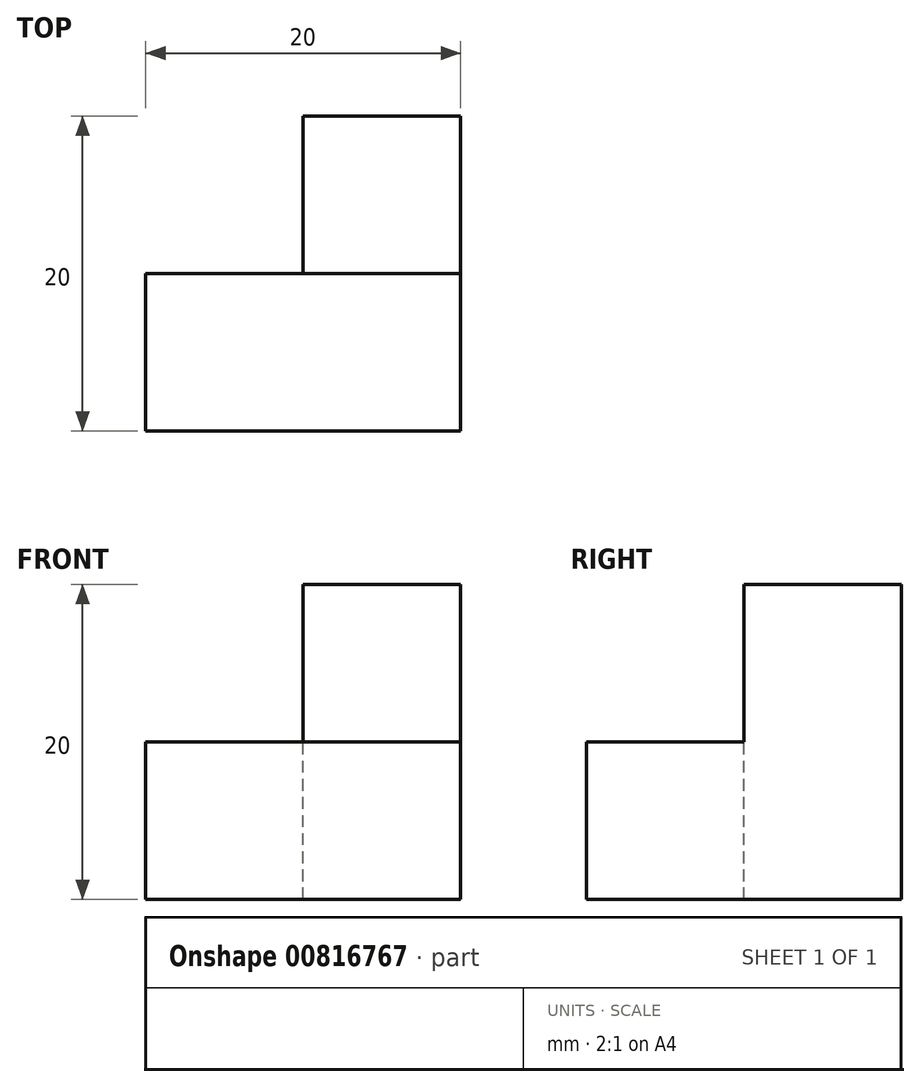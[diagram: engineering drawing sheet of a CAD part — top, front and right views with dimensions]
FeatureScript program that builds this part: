
annotation { "Feature Type Name" : "Feature", "Feature Type Description" : "" }
export const myFeature = defineFeature(function(context is Context, id is Id, definition is map)
    precondition{}
    {
        {
            var Q0;
            Q0=qCreatedBy(makeId("Top.planeOp"),FACE);
            var sketch = newSketch(context, id + "F0", { "sketchPlane" : qUnion([Q0])});
            skLineSegment(sketch, "E0.bottom", {"start": v(0, 0) * mm, "end": v(10, 0) * mm});
            skLineSegment(sketch, "E0.top", {"start": v(0, 10) * mm, "end": v(10, 10) * mm});
            skLineSegment(sketch, "E0.left", {"start": v(0, 0) * mm, "end": v(0, 10) * mm});
            skLineSegment(sketch, "E0.right", {"start": v(10, 0) * mm, "end": v(10, 10) * mm});
            skSolve(sketch);
        }
        {
            var Q0;
            Q0=makeQuery(id+"F0.imprint","IMPRINT",FACE,{"disambiguationData":[TD([[makeQuery(id+"F0.imprint","IMPRINT",EDGE,{"derivedFrom":sQuery(id+"F0.wireOp",EDGE,"E0.bottom")}),1.0]])]});
            extrude(context, id + "F1", {"entities" : qUnion([Q0]), "depth" : 20 * mm, "offsetDistance" : 25 * mm});
        }
        {
            var Q0;
            Q0=makeQuery(id+"F1.opExtrude","SWEPT_FACE",FACE,{"disambiguationData":[OSD([sQuery(id+"F0.wireOp",EDGE,"E0.bottom")])]});
            var sketch = newSketch(context, id + "F2", { "sketchPlane" : qUnion([Q0])});
            skLineSegment(sketch, "E1.bottom", {"start": v(10, 0) * mm, "end": v(0, 0) * mm});
            skLineSegment(sketch, "E1.top", {"start": v(10, 10) * mm, "end": v(0, 10) * mm});
            skLineSegment(sketch, "E1.left", {"start": v(10, 0) * mm, "end": v(10, 10) * mm});
            skLineSegment(sketch, "E1.right", {"start": v(0, 0) * mm, "end": v(0, 10) * mm});
            skSolve(sketch);
        }
        {
            var Q0;
            Q0=makeQuery(id+"F2.imprint","IMPRINT",FACE,{"disambiguationData":[TD([[makeQuery(id+"F2.imprint","IMPRINT",EDGE,{"derivedFrom":sQuery(id+"F2.wireOp",EDGE,"E1.bottom")}),1.0]])]});
            extrude(context, id + "F3", {"entities" : qUnion([Q0]), "operationType" : NewBodyOperationType.ADD, "depth" : 10 * mm, "offsetDistance" : 25 * mm});
        }
        {
            var Q0;
            Q0=makeQuery(id+"F3.boolean.opBoolean","MERGE",FACE,{"derivedFrom":[makeQuery(id+"F1.opExtrude","SWEPT_FACE",FACE,{"disambiguationData":[OSD([sQuery(id+"F0.wireOp",EDGE,"E0.left")])]}),makeQuery(id+"F3.opExtrude","SWEPT_FACE",FACE,{"disambiguationData":[OSD([sQuery(id+"F2.wireOp",EDGE,"E1.right")])]})]});
            var sketch = newSketch(context, id + "F4", { "sketchPlane" : qUnion([Q0])});
            skLineSegment(sketch, "E2.bottom", {"start": v(0, 0) * mm, "end": v(10, 0) * mm});
            skLineSegment(sketch, "E2.top", {"start": v(0, 10) * mm, "end": v(10, 10) * mm});
            skLineSegment(sketch, "E2.left", {"start": v(0, 0) * mm, "end": v(0, 10) * mm});
            skLineSegment(sketch, "E2.right", {"start": v(10, 0) * mm, "end": v(10, 10) * mm});
            skSolve(sketch);
        }
        {
            var Q0;
            Q0=makeQuery(id+"F4.imprint","IMPRINT",FACE,{"disambiguationData":[TD([[makeQuery(id+"F4.imprint","IMPRINT",EDGE,{"derivedFrom":sQuery(id+"F4.wireOp",EDGE,"E2.bottom")}),-1.0]])]});
            extrude(context, id + "F5", {"entities" : qUnion([Q0]), "operationType" : NewBodyOperationType.ADD, "depth" : 10 * mm, "offsetDistance" : 25 * mm});
        }
    });
